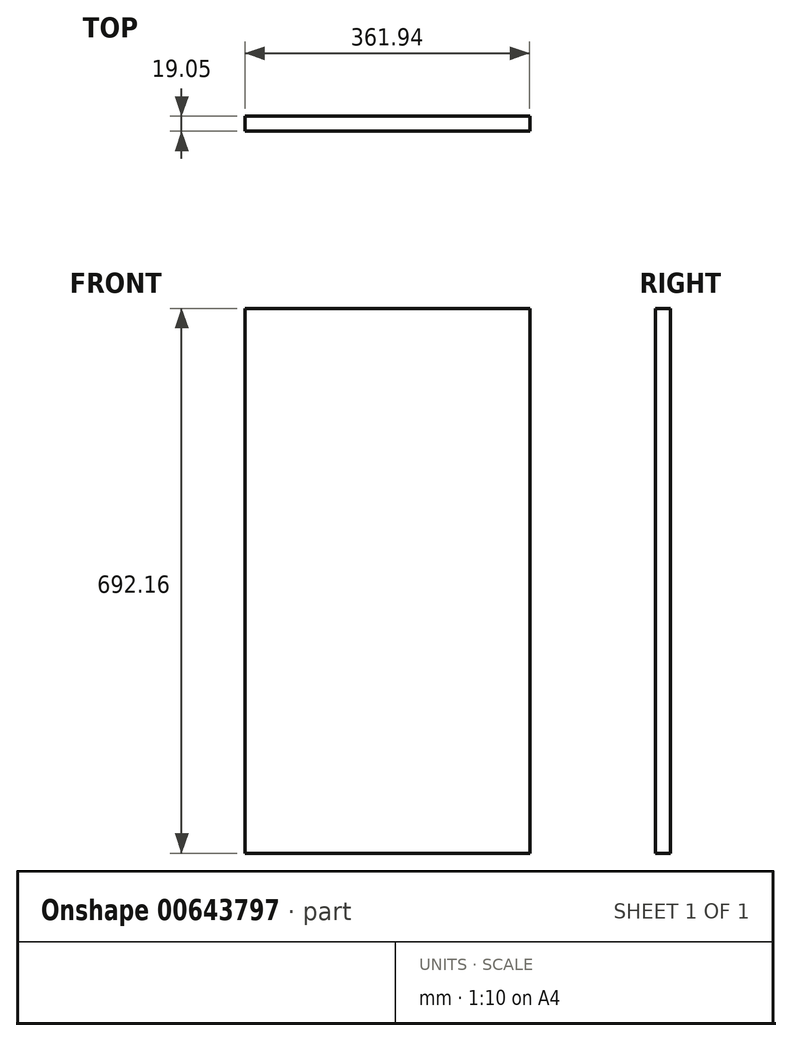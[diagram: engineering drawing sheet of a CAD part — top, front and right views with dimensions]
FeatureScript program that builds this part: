
annotation { "Feature Type Name" : "Feature", "Feature Type Description" : "" }
export const myFeature = defineFeature(function(context is Context, id is Id, definition is map)
    precondition{}
    {
        {
            var Q0;
            Q0=qCreatedBy(makeId("Front.planeOp"),FACE);
            var sketch = newSketch(context, id + "F0", { "sketchPlane" : qUnion([Q0])});
            skLineSegment(sketch, "E0.bottom", {"start": v(-180.97, 346.08) * mm, "end": v(180.98, 346.08) * mm});
            skLineSegment(sketch, "E0.top", {"start": v(-180.98, -346.08) * mm, "end": v(180.97, -346.08) * mm});
            skLineSegment(sketch, "E0.left", {"start": v(-180.97, 346.08) * mm, "end": v(-180.98, -346.08) * mm});
            skLineSegment(sketch, "E0.right", {"start": v(180.98, 346.07) * mm, "end": v(180.97, -346.08) * mm});
            skPoint(sketch, "E0.middle", {"position": v(0, 0) * mm});
            skSolve(sketch);
        }
        {
            var Q0;
            Q0=makeQuery(id+"F0.imprint","IMPRINT",FACE,{"disambiguationData":[TD([[makeQuery(id+"F0.imprint","IMPRINT",EDGE,{"derivedFrom":sQuery(id+"F0.wireOp",EDGE,"E0.bottom")}),-1.0]])]});
            extrude(context, id + "F1", {"entities" : qUnion([Q0]), "depth" : 19.05 * mm, "offsetDistance" : 25.4 * mm});
        }
    });
